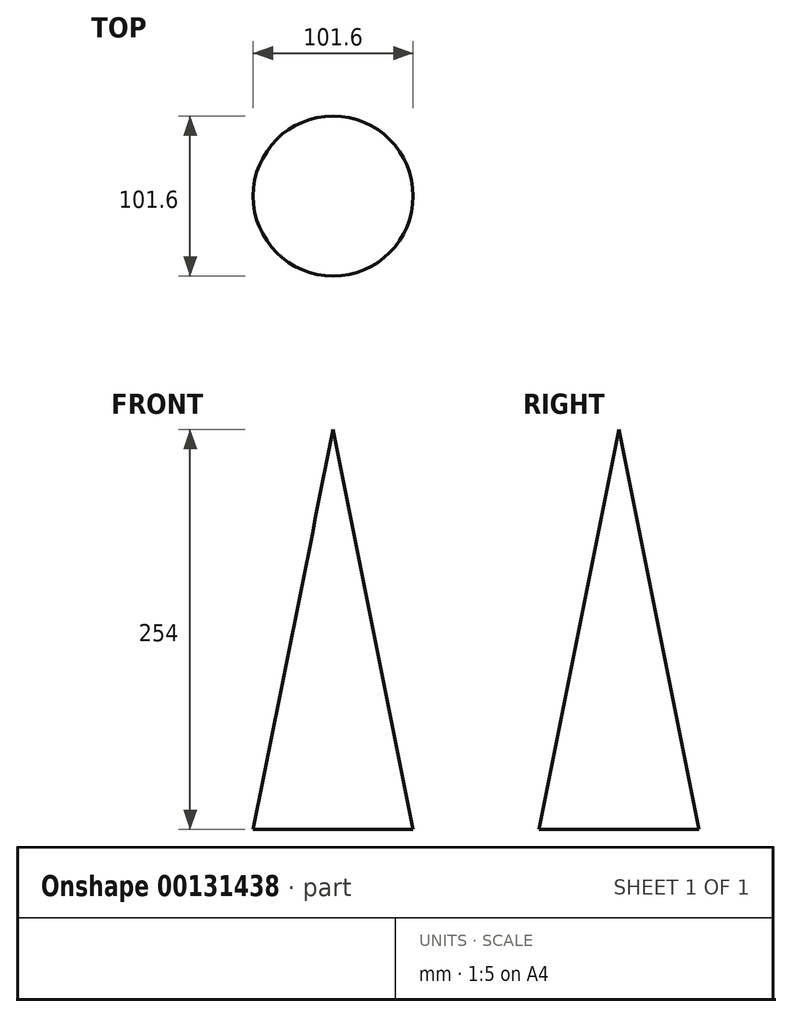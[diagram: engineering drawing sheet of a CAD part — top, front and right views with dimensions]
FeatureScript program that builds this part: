
annotation { "Feature Type Name" : "Feature", "Feature Type Description" : "" }
export const myFeature = defineFeature(function(context is Context, id is Id, definition is map)
    precondition{}
    {
        {
            var Q0;
            Q0=qCreatedBy(makeId("Front.planeOp"),FACE);
            var sketch = newSketch(context, id + "F0", { "sketchPlane" : qUnion([Q0])});
            skLineSegment(sketch, "E0", {"start": v(0, 0) * mm, "end": v(50.8, 0) * mm});
            skLineSegment(sketch, "E1", {"start": v(50.8, 0) * mm, "end": v(0, 254) * mm});
            skLineSegment(sketch, "E2", {"start": v(0, 0) * mm, "end": v(0, 254) * mm});
            skSolve(sketch);
        }
        {
            var Q0;
            Q0=makeQuery(id+"F0.imprint","IMPRINT",FACE,{"disambiguationData":[TD([[makeQuery(id+"F0.imprint","IMPRINT",EDGE,{"derivedFrom":sQuery(id+"F0.wireOp",EDGE,"E0")}),1.0]])]});
            var Q1;
            Q1=sQuery(id+"F0.wireOp",EDGE,"E2");
            revolve(context, id + "F1", {"entities" : qUnion([Q0]), "axis" : qUnion([Q1]), "revolveType" : RevolveType.FULL});
        }
    });
